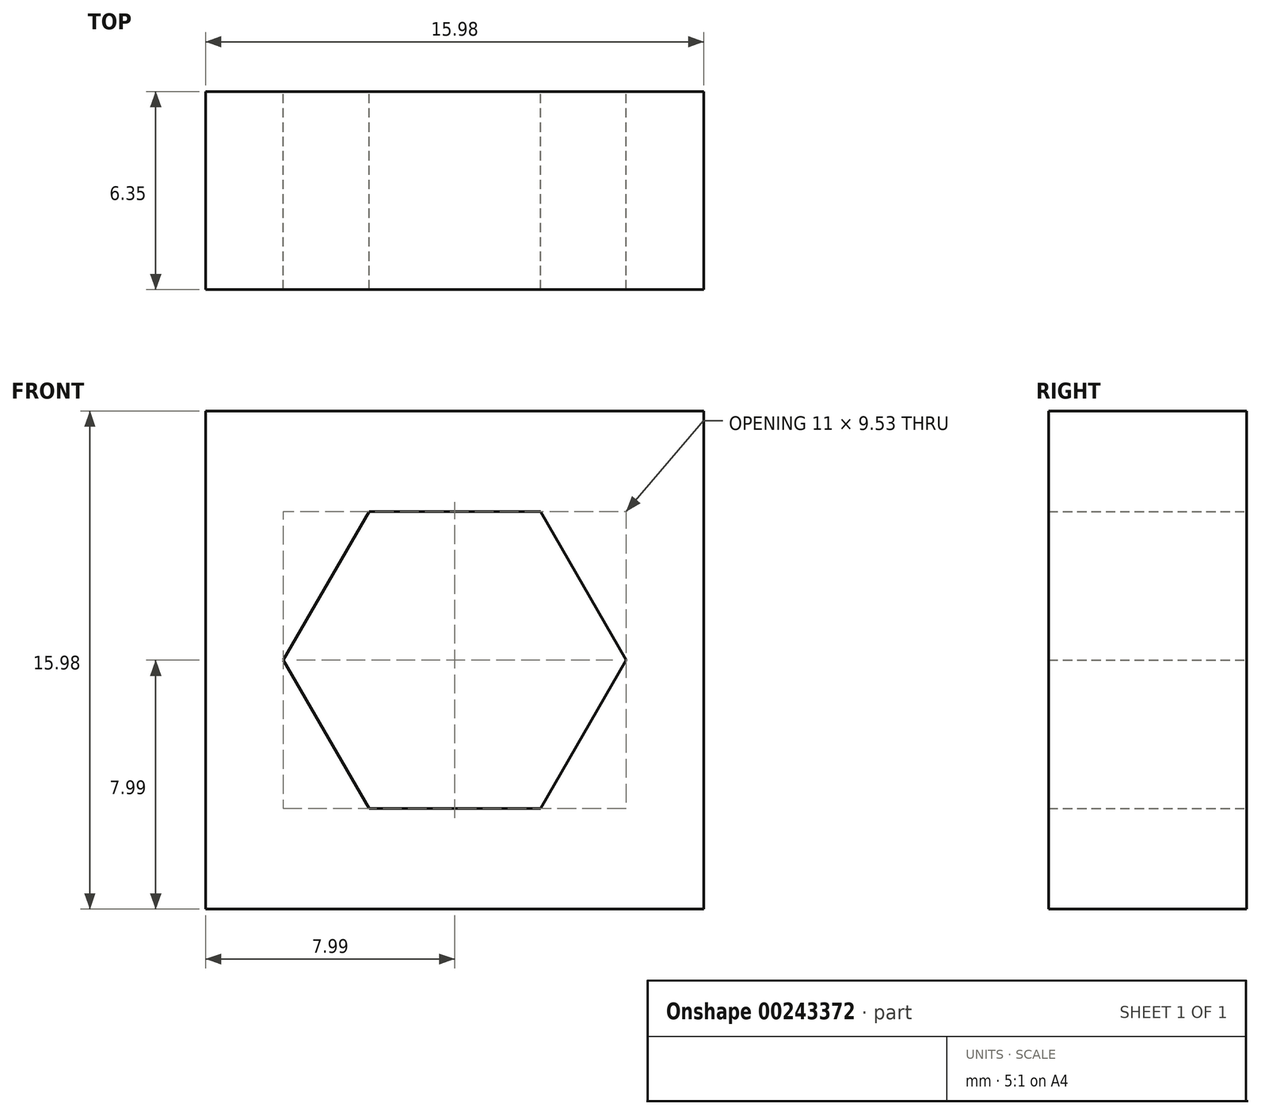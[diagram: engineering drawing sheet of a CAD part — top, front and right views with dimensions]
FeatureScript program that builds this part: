
annotation { "Feature Type Name" : "Feature", "Feature Type Description" : "" }
export const myFeature = defineFeature(function(context is Context, id is Id, definition is map)
    precondition{}
    {
        {
            var Q0;
            Q0=qCreatedBy(makeId("Front.planeOp"),FACE);
            var sketch = newSketch(context, id + "F0", { "sketchPlane" : qUnion([Q0])});
            skCircle(sketch, "E0.cCircle", {"center": v(0, 0) * mm, "radius": 4.76 * mm, "construction": true});
            skLineSegment(sketch, "E0.0", {"start": v(-5.5, 0) * mm, "end": v(-2.75, 4.76) * mm});
            skLineSegment(sketch, "E0.1", {"start": v(-2.75, 4.76) * mm, "end": v(2.75, 4.76) * mm});
            skLineSegment(sketch, "E0.2", {"start": v(2.75, 4.76) * mm, "end": v(5.5, 0) * mm});
            skLineSegment(sketch, "E0.3", {"start": v(5.5, 0) * mm, "end": v(2.75, -4.76) * mm});
            skLineSegment(sketch, "E0.4", {"start": v(2.75, -4.76) * mm, "end": v(-2.75, -4.76) * mm});
            skLineSegment(sketch, "E0.5", {"start": v(-2.75, -4.76) * mm, "end": v(-5.5, 0) * mm});
            skPoint(sketch, "E0.0.midPoint", {"position": v(-4.12, 2.38) * mm});
            skLineSegment(sketch, "E1.bottom", {"start": v(-7.99, 7.99) * mm, "end": v(7.99, 7.99) * mm});
            skLineSegment(sketch, "E1.top", {"start": v(-7.99, -7.99) * mm, "end": v(7.99, -7.99) * mm});
            skLineSegment(sketch, "E1.left", {"start": v(-7.99, 7.99) * mm, "end": v(-7.99, -7.99) * mm});
            skLineSegment(sketch, "E1.right", {"start": v(7.99, 7.99) * mm, "end": v(7.99, -7.99) * mm});
            skSolve(sketch);
        }
        {
            var Q0;
            Q0 = qSketchRegion(id + "F0", true);
            extrude(context, id + "F1", {"entities" : qUnion([Q0]), "depth" : 6.35 * mm});
        }
    });
